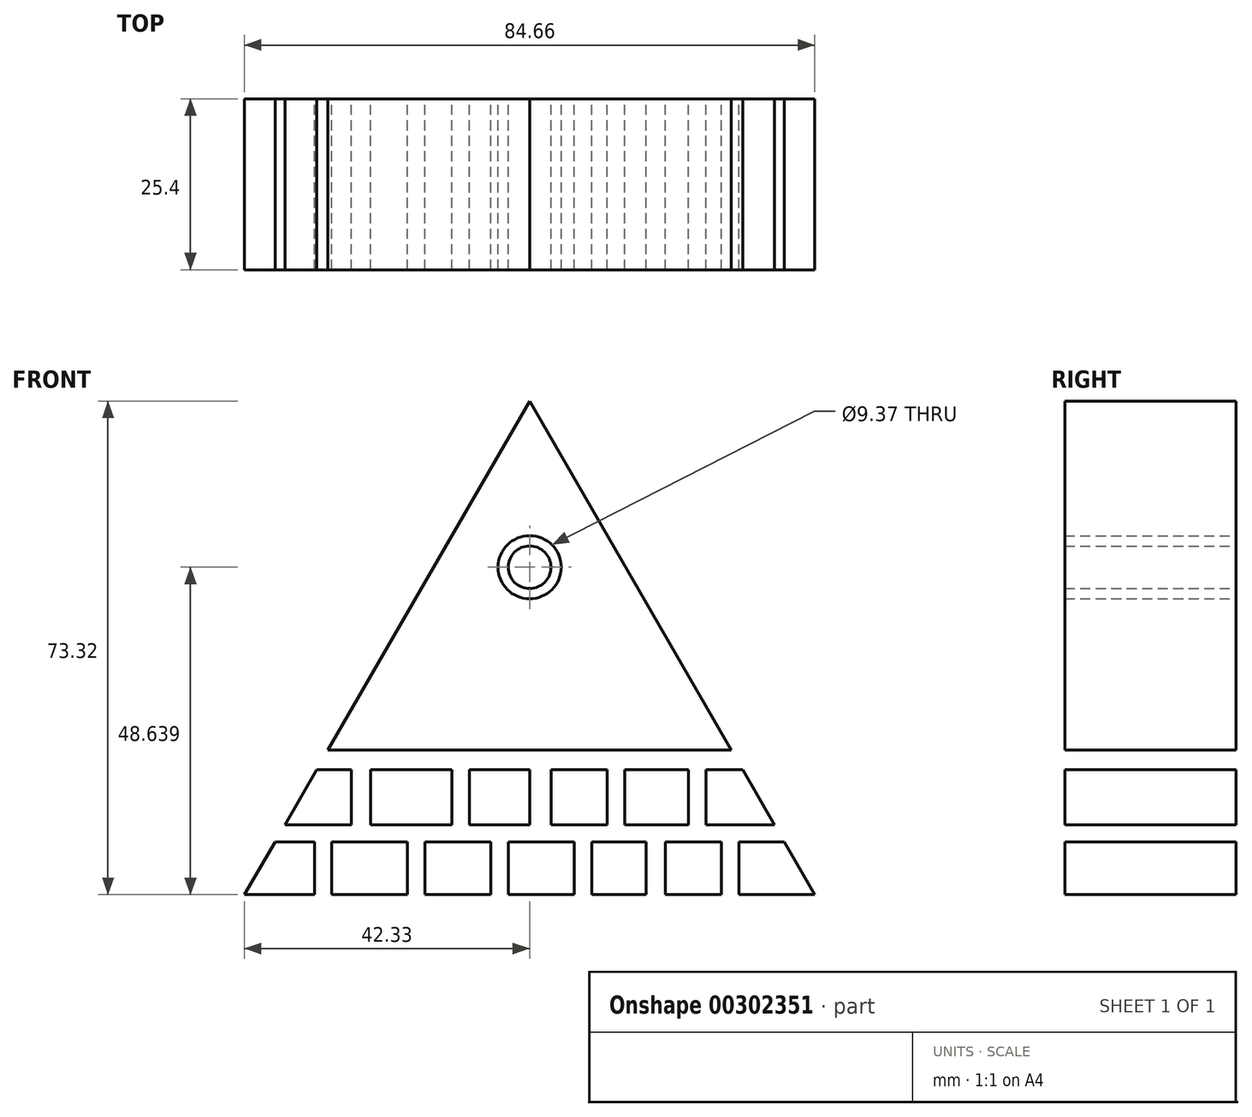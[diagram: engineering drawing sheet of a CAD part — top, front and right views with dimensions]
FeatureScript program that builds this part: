
annotation { "Feature Type Name" : "Feature", "Feature Type Description" : "" }
export const myFeature = defineFeature(function(context is Context, id is Id, definition is map)
    precondition{}
    {
        {
            var Q0;
            Q0=qCreatedBy(makeId("Front.planeOp"),FACE);
            var sketch = newSketch(context, id + "F0", { "sketchPlane" : qUnion([Q0])});
            skLineSegment(sketch, "E0", {"start": v(0, 73.32) * mm, "end": v(-42.33, 0) * mm});
            skLineSegment(sketch, "E1", {"start": v(-42.33, 0) * mm, "end": v(42.33, 0) * mm});
            skLineSegment(sketch, "E2", {"start": v(0, 73.32) * mm, "end": v(42.33, 0) * mm});
            skFitSpline(sketch, "E3", {"points": [v(15.2, 47) * mm, v(-15.05, 47.25) * mm], "startDerivative": vector(-45.58, 31.69) * mm, "endDerivative": vector(-45.15, -30.94) * mm});
            skFitSpline(sketch, "E4", {"points": [v(-15.05, 47.25) * mm, v(15.2, 47) * mm], "startDerivative": vector(46.01, -19.14) * mm, "endDerivative": vector(44.72, 18.4) * mm});
            skCircle(sketch, "E5", {"center": v(0, 48.64) * mm, "radius": 4.69 * mm});
            skLineSegment(sketch, "E6", {"start": v(31.61, 18.56) * mm, "end": v(-31.61, 18.56) * mm});
            skLineSegment(sketch, "E7", {"start": v(-36.33, 10.4) * mm, "end": v(36.33, 10.4) * mm});
            skLineSegment(sketch, "E8", {"start": v(-23.6, 18.56) * mm, "end": v(-23.6, 10.4) * mm});
            skLineSegment(sketch, "E9", {"start": v(-29.36, 10.4) * mm, "end": v(-29.36, 0) * mm});
            skLineSegment(sketch, "E10", {"start": v(-15.54, 10.4) * mm, "end": v(-15.54, 0) * mm});
            skLineSegment(sketch, "E11", {"start": v(-8.92, 18.56) * mm, "end": v(-8.92, 10.4) * mm});
            skLineSegment(sketch, "E12", {"start": v(-3.17, 10.4) * mm, "end": v(-3.17, 0) * mm});
            skLineSegment(sketch, "E13", {"start": v(3.17, 18.56) * mm, "end": v(3.17, 10.4) * mm});
            skLineSegment(sketch, "E14", {"start": v(9.2, 10.4) * mm, "end": v(9.2, 0) * mm});
            skLineSegment(sketch, "E15", {"start": v(14.1, 18.56) * mm, "end": v(14.1, 10.4) * mm});
            skLineSegment(sketch, "E16", {"start": v(20.15, 10.4) * mm, "end": v(20.15, 0) * mm});
            skLineSegment(sketch, "E17", {"start": v(26.2, 18.56) * mm, "end": v(26.2, 10.4) * mm});
            skLineSegment(sketch, "E18", {"start": v(31.08, 10.4) * mm, "end": v(31.08, 0) * mm});
            skCircle(sketch, "E19", {"center": v(0, 48.64) * mm, "radius": 3.17 * mm});
            skLineSegment(sketch, "E20", {"start": v(-26.48, 18.56) * mm, "end": v(-26.48, 10.4) * mm});
            skLineSegment(sketch, "E21", {"start": v(-31.95, 10.4) * mm, "end": v(-31.95, 0) * mm});
            skLineSegment(sketch, "E22", {"start": v(-18.13, 10.4) * mm, "end": v(-18.13, 0) * mm});
            skLineSegment(sketch, "E23", {"start": v(-11.51, 18.56) * mm, "end": v(-11.51, 10.4) * mm});
            skLineSegment(sketch, "E24", {"start": v(-5.76, 10.4) * mm, "end": v(-5.76, 0) * mm});
            skLineSegment(sketch, "E25", {"start": v(0, 18.56) * mm, "end": v(0, 10.4) * mm});
            skLineSegment(sketch, "E26", {"start": v(6.62, 10.4) * mm, "end": v(6.62, 0) * mm});
            skLineSegment(sketch, "E27", {"start": v(11.51, 18.56) * mm, "end": v(11.51, 10.4) * mm});
            skLineSegment(sketch, "E28", {"start": v(17.27, 10.4) * mm, "end": v(17.27, 0) * mm});
            skLineSegment(sketch, "E29", {"start": v(23.6, 18.56) * mm, "end": v(23.6, 10.4) * mm});
            skLineSegment(sketch, "E30", {"start": v(28.5, 10.4) * mm, "end": v(28.5, 0) * mm});
            skLineSegment(sketch, "E31", {"start": v(-37.79, 7.86) * mm, "end": v(37.79, 7.86) * mm});
            skLineSegment(sketch, "E32", {"start": v(-40.72, 2.8) * mm, "end": v(40.72, 2.8) * mm});
            skLineSegment(sketch, "E33", {"start": v(-29.94, 21.47) * mm, "end": v(29.94, 21.47) * mm});
            skSolve(sketch);
        }
        {
            var Q0;
            {var subQ4=sQuery(id+"F0.wireOp",EDGE,"E3");Q0=makeQuery(id+"F0.imprint","IMPRINT",FACE,{"disambiguationData":[TD([[makeQuery(id+"F0.imprint","IMPRINT",EDGE,{"derivedFrom":subQ4}),-1.0]])]});}
            var Q1;
            {var subQ0=sQuery(id+"F0.wireOp",EDGE,"E4");Q1=makeQuery(id+"F0.imprint","IMPRINT",FACE,{"disambiguationData":[TD([[makeQuery(id+"F0.imprint","IMPRINT",EDGE,{"derivedFrom":subQ0}),-1.0]])]});}
            var Q2;
            {var subQ0=sQuery(id+"F0.wireOp",EDGE,"E1");var subQ1=sQuery(id+"F0.wireOp",EDGE,"E0");var subQ2=makeQuery(id+"F0.imprint","INTERSECT",VERTEX,{"derivedFrom":[subQ1,subQ0]});Q2=makeQuery(id+"F0.imprint","IMPRINT",FACE,{"disambiguationData":[TD([[makeQuery(id+"F0.imprint","IMPRINT",EDGE,{"disambiguationData":[TD([[subQ2,1.0]])],"derivedFrom":subQ1}),1.0]])]});}
            var Q3;
            {var subQ0=sQuery(id+"F0.wireOp",EDGE,"E2");var subQ1=sQuery(id+"F0.wireOp",EDGE,"E1");var subQ2=makeQuery(id+"F0.imprint","INTERSECT",VERTEX,{"derivedFrom":[subQ1,subQ0]});Q3=makeQuery(id+"F0.imprint","IMPRINT",FACE,{"disambiguationData":[TD([[makeQuery(id+"F0.imprint","IMPRINT",EDGE,{"disambiguationData":[TD([[subQ2,1.0]])],"derivedFrom":subQ1}),1.0]])]});}
            var Q4;
            {var subQ0=sQuery(id+"F0.wireOp",EDGE,"E31");var subQ1=sQuery(id+"F0.wireOp",EDGE,"E0");var subQ2=makeQuery(id+"F0.imprint","INTERSECT",VERTEX,{"derivedFrom":[subQ1,subQ0]});Q4=makeQuery(id+"F0.imprint","IMPRINT",FACE,{"disambiguationData":[TD([[makeQuery(id+"F0.imprint","IMPRINT",EDGE,{"disambiguationData":[TD([[subQ2,-1.0]])],"derivedFrom":subQ1}),1.0]])]});}
            var Q5;
            {var subQ0=sQuery(id+"F0.wireOp",EDGE,"E9");var subQ1=sQuery(id+"F0.wireOp",EDGE,"E1");var subQ2=makeQuery(id+"F0.imprint","INTERSECT",VERTEX,{"derivedFrom":[subQ1,subQ0]});Q5=makeQuery(id+"F0.imprint","IMPRINT",FACE,{"disambiguationData":[TD([[makeQuery(id+"F0.imprint","IMPRINT",EDGE,{"disambiguationData":[TD([[subQ2,-1.0]])],"derivedFrom":subQ1}),1.0]])]});}
            var Q6;
            {var subQ0=sQuery(id+"F0.wireOp",EDGE,"E10");var subQ1=sQuery(id+"F0.wireOp",EDGE,"E1");var subQ2=makeQuery(id+"F0.imprint","INTERSECT",VERTEX,{"derivedFrom":[subQ1,subQ0]});Q6=makeQuery(id+"F0.imprint","IMPRINT",FACE,{"disambiguationData":[TD([[makeQuery(id+"F0.imprint","IMPRINT",EDGE,{"disambiguationData":[TD([[subQ2,-1.0]])],"derivedFrom":subQ1}),1.0]])]});}
            var Q7;
            {var subQ0=sQuery(id+"F0.wireOp",EDGE,"E12");var subQ1=sQuery(id+"F0.wireOp",EDGE,"E1");var subQ2=makeQuery(id+"F0.imprint","INTERSECT",VERTEX,{"derivedFrom":[subQ1,subQ0]});Q7=makeQuery(id+"F0.imprint","IMPRINT",FACE,{"disambiguationData":[TD([[makeQuery(id+"F0.imprint","IMPRINT",EDGE,{"disambiguationData":[TD([[subQ2,-1.0]])],"derivedFrom":subQ1}),1.0]])]});}
            var Q8;
            {var subQ0=sQuery(id+"F0.wireOp",EDGE,"E14");var subQ1=sQuery(id+"F0.wireOp",EDGE,"E1");var subQ2=makeQuery(id+"F0.imprint","INTERSECT",VERTEX,{"derivedFrom":[subQ1,subQ0]});Q8=makeQuery(id+"F0.imprint","IMPRINT",FACE,{"disambiguationData":[TD([[makeQuery(id+"F0.imprint","IMPRINT",EDGE,{"disambiguationData":[TD([[subQ2,-1.0]])],"derivedFrom":subQ1}),1.0]])]});}
            var Q9;
            {var subQ0=sQuery(id+"F0.wireOp",EDGE,"E16");var subQ1=sQuery(id+"F0.wireOp",EDGE,"E1");var subQ2=makeQuery(id+"F0.imprint","INTERSECT",VERTEX,{"derivedFrom":[subQ1,subQ0]});Q9=makeQuery(id+"F0.imprint","IMPRINT",FACE,{"disambiguationData":[TD([[makeQuery(id+"F0.imprint","IMPRINT",EDGE,{"disambiguationData":[TD([[subQ2,-1.0]])],"derivedFrom":subQ1}),1.0]])]});}
            var Q10;
            {var subQ0=sQuery(id+"F0.wireOp",EDGE,"E31");var subQ1=sQuery(id+"F0.wireOp",EDGE,"E2");var subQ2=makeQuery(id+"F0.imprint","INTERSECT",VERTEX,{"derivedFrom":[subQ1,subQ0]});Q10=makeQuery(id+"F0.imprint","IMPRINT",FACE,{"disambiguationData":[TD([[makeQuery(id+"F0.imprint","IMPRINT",EDGE,{"disambiguationData":[TD([[subQ2,-1.0]])],"derivedFrom":subQ1}),-1.0]])]});}
            var Q11;
            Q11=makeQuery(id+"F0.imprint","IMPRINT",FACE,{"disambiguationData":[TD([[makeQuery(id+"F0.imprint","IMPRINT",EDGE,{"derivedFrom":sQuery(id+"F0.wireOp",EDGE,"E3")}),1.0]])]});
            var Q12;
            {var subQ7=sQuery(id+"F0.wireOp",EDGE,"E20");Q12=makeQuery(id+"F0.imprint","IMPRINT",FACE,{"disambiguationData":[TD([[makeQuery(id+"F0.imprint","IMPRINT",EDGE,{"derivedFrom":subQ7}),-1.0]])]});}
            var Q13;
            {var subQ3=sQuery(id+"F0.wireOp",EDGE,"E17");Q13=makeQuery(id+"F0.imprint","IMPRINT",FACE,{"disambiguationData":[TD([[makeQuery(id+"F0.imprint","IMPRINT",EDGE,{"derivedFrom":subQ3}),1.0]])]});}
            var Q14;
            {var subQ4=sQuery(id+"F0.wireOp",EDGE,"E8");Q14=makeQuery(id+"F0.imprint","IMPRINT",FACE,{"disambiguationData":[TD([[makeQuery(id+"F0.imprint","IMPRINT",EDGE,{"derivedFrom":subQ4}),1.0]])]});}
            var Q15;
            {var subQ3=sQuery(id+"F0.wireOp",EDGE,"E11");Q15=makeQuery(id+"F0.imprint","IMPRINT",FACE,{"disambiguationData":[TD([[makeQuery(id+"F0.imprint","IMPRINT",EDGE,{"derivedFrom":subQ3}),1.0]])]});}
            var Q16;
            {var subQ3=sQuery(id+"F0.wireOp",EDGE,"E13");Q16=makeQuery(id+"F0.imprint","IMPRINT",FACE,{"disambiguationData":[TD([[makeQuery(id+"F0.imprint","IMPRINT",EDGE,{"derivedFrom":subQ3}),1.0]])]});}
            var Q17;
            {var subQ4=sQuery(id+"F0.wireOp",EDGE,"E15");Q17=makeQuery(id+"F0.imprint","IMPRINT",FACE,{"disambiguationData":[TD([[makeQuery(id+"F0.imprint","IMPRINT",EDGE,{"derivedFrom":subQ4}),1.0]])]});}
            var Q18;
            {var subQ0=sQuery(id+"F0.wireOp",EDGE,"E31");var subQ1=sQuery(id+"F0.wireOp",EDGE,"E14");var subQ2=makeQuery(id+"F0.imprint","INTERSECT",VERTEX,{"derivedFrom":[subQ1,subQ0]});Q18=makeQuery(id+"F0.imprint","IMPRINT",FACE,{"disambiguationData":[TD([[makeQuery(id+"F0.imprint","IMPRINT",EDGE,{"disambiguationData":[TD([[subQ2,-1.0]])],"derivedFrom":subQ1}),1.0]])]});}
            var Q19;
            {var subQ0=sQuery(id+"F0.wireOp",EDGE,"E31");var subQ1=sQuery(id+"F0.wireOp",EDGE,"E16");var subQ2=makeQuery(id+"F0.imprint","INTERSECT",VERTEX,{"derivedFrom":[subQ1,subQ0]});Q19=makeQuery(id+"F0.imprint","IMPRINT",FACE,{"disambiguationData":[TD([[makeQuery(id+"F0.imprint","IMPRINT",EDGE,{"disambiguationData":[TD([[subQ2,-1.0]])],"derivedFrom":subQ1}),1.0]])]});}
            var Q20;
            {var subQ0=sQuery(id+"F0.wireOp",EDGE,"E31");var subQ1=sQuery(id+"F0.wireOp",EDGE,"E12");var subQ2=makeQuery(id+"F0.imprint","INTERSECT",VERTEX,{"derivedFrom":[subQ1,subQ0]});Q20=makeQuery(id+"F0.imprint","IMPRINT",FACE,{"disambiguationData":[TD([[makeQuery(id+"F0.imprint","IMPRINT",EDGE,{"disambiguationData":[TD([[subQ2,-1.0]])],"derivedFrom":subQ1}),1.0]])]});}
            var Q21;
            {var subQ0=sQuery(id+"F0.wireOp",EDGE,"E31");var subQ1=sQuery(id+"F0.wireOp",EDGE,"E10");var subQ2=makeQuery(id+"F0.imprint","INTERSECT",VERTEX,{"derivedFrom":[subQ1,subQ0]});Q21=makeQuery(id+"F0.imprint","IMPRINT",FACE,{"disambiguationData":[TD([[makeQuery(id+"F0.imprint","IMPRINT",EDGE,{"disambiguationData":[TD([[subQ2,-1.0]])],"derivedFrom":subQ1}),1.0]])]});}
            var Q22;
            {var subQ0=sQuery(id+"F0.wireOp",EDGE,"E31");var subQ1=sQuery(id+"F0.wireOp",EDGE,"E9");var subQ2=makeQuery(id+"F0.imprint","INTERSECT",VERTEX,{"derivedFrom":[subQ1,subQ0]});Q22=makeQuery(id+"F0.imprint","IMPRINT",FACE,{"disambiguationData":[TD([[makeQuery(id+"F0.imprint","IMPRINT",EDGE,{"disambiguationData":[TD([[subQ2,-1.0]])],"derivedFrom":subQ1}),1.0]])]});}
            var Q23;
            Q23=makeQuery(id+"F0.imprint","IMPRINT",FACE,{"disambiguationData":[TD([[makeQuery(id+"F0.imprint","IMPRINT",EDGE,{"derivedFrom":sQuery(id+"F0.wireOp",EDGE,"E19")}),1.0]])]});
            extrude(context, id + "F1", {"entities" : qUnion([Q0, Q1, Q2, Q3, Q4, Q5, Q6, Q7, Q8, Q9, Q10, Q11, Q12, Q13, Q14, Q15, Q16, Q17, Q18, Q19, Q20, Q21, Q22, Q23]), "depth" : 25.4 * mm});
        }
    });
